# Revit family: PV Oberteil - Blitz -und Überspannungsableiter Typ 1+2_Typ 2
name_source: partatom
category: Generic Models
revit_build: Autodesk Revit 2015 (Build: 20140606_1530(x64)
units: mm (PartAtom-declared; Revit-internal decimal feet)

## types (4) — shared parameters
Height = 48 mm  [stored 0.15748 ft]
Length = 18 mm
Manufacturer = OBO Bettermann
Material 2 = Steel
URL = http://www.obo-bettermann.com
Width = 45 mm

## per-type parameters (varying)
| type | GTIN | Manufacturer Art.No. | Material |
| V50-B+C 0-300PV | 4012195708841 | 5093726 | OBO PA 6 GF20 RAL 2003 |
| V25-B+C 0-450PV | 4012195708896 | 5097065 | OBO PA 6 GF20 RAL 2003 |
| V20-C 0-300PV | 4012195708902 | 5099611 | OBO PA 6 GF20 RAL 7035 |
| V20-C 0-500PV | 4012195708933 | 5099708 | OBO PA 6 GF20 RAL 7035 |

note: column(s) folded — value = type name in every type: Article Type

note: [stored X ft] marks values corroborated as IEEE doubles in the binary element streams (Revit-internal decimal feet)

## geometry (parser evidence)
native form markers: Sweep x2
no freeform markers — native parametric forms only
